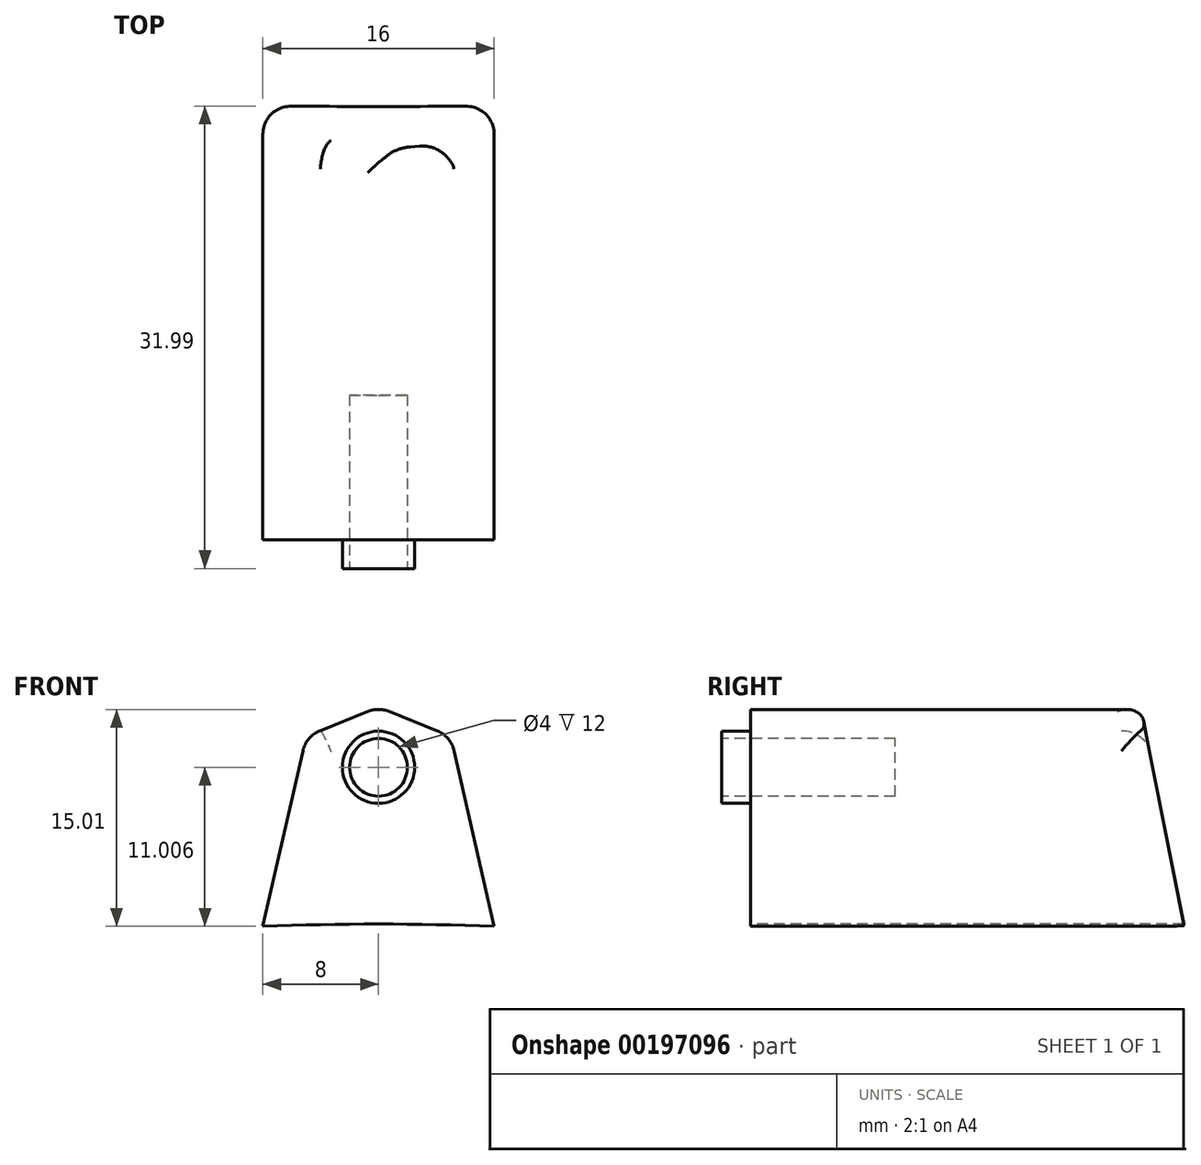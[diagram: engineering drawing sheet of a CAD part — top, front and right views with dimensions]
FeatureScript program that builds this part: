
annotation { "Feature Type Name" : "Feature", "Feature Type Description" : "" }
export const myFeature = defineFeature(function(context is Context, id is Id, definition is map)
    precondition{}
    {
        {
            var Q0;
            Q0=qCreatedBy(makeId("Front.planeOp"),FACE);
            var sketch = newSketch(context, id + "F0", { "sketchPlane" : qUnion([Q0])});
            skArc(sketch, "E0", {"start": v(8, 203.04) * mm, "mid": v(0, 203.2) * mm, "end": v(-8, 203.04) * mm});
            skLineSegment(sketch, "E1", {"start": v(0, 218.2) * mm, "end": v(5, 216.2) * mm});
            skLineSegment(sketch, "E2", {"start": v(5, 216.2) * mm, "end": v(8, 203.04) * mm});
            skLineSegment(sketch, "E3", {"start": v(0, 0) * mm, "end": v(0, 156.59) * mm, "construction": true});
            skLineSegment(sketch, "E4.MirrorCS", {"start": v(-5, 216.2) * mm, "end": v(-8, 203.04) * mm});
            skLineSegment(sketch, "E5.MirrorCS", {"start": v(0, 218.2) * mm, "end": v(-5, 216.2) * mm});
            skSolve(sketch);
        }
        {
            var Q0;
            Q0=makeQuery(id+"F0.imprint","IMPRINT",FACE,{"disambiguationData":[TD([[makeQuery(id+"F0.imprint","IMPRINT",EDGE,{"derivedFrom":sQuery(id+"F0.wireOp",EDGE,"E0")}),-1.0]])]});
            extrude(context, id + "F1", {"entities" : qUnion([Q0]), "oppositeDirection" : true, "depth" : 30 * mm});
        }
        {
            var Q0;
            Q0=qCreatedBy(makeId("Right.planeOp"),FACE);
            var sketch = newSketch(context, id + "F2", { "sketchPlane" : qUnion([Q0])});
            skLineSegment(sketch, "E6.0", {"start": v(30, 203.04) * mm, "end": v(0, 203.04) * mm});
            skLineSegment(sketch, "E7.0", {"start": v(30, 218.2) * mm, "end": v(0, 218.2) * mm});
            skLineSegment(sketch, "E8", {"start": v(30, 203.04) * mm, "end": v(27, 218.2) * mm});
            skLineSegment(sketch, "E9", {"start": v(30, 203.04) * mm, "end": v(30, 218.2) * mm});
            skSolve(sketch);
        }
        {
            var Q0;
            Q0 = qSketchRegion(id + "F2", true);
            extrude(context, id + "F3", {"entities" : qUnion([Q0]), "operationType" : NewBodyOperationType.REMOVE, "endBound" : BoundingType.SYMMETRIC, "depth" : 25 * mm});
        }
        {
            var Q0;
            Q0=makeQuery(id+"F1.opExtrude","SWEPT_EDGE",EDGE,{"disambiguationData":[OSD([sQuery(id+"F0.wireOp",EDGE,"E1"),sQuery(id+"F0.wireOp",EDGE,"E2")])]});
            var Q1;
            Q1=makeQuery(id+"F1.opExtrude","SWEPT_EDGE",EDGE,{"disambiguationData":[OSD([sQuery(id+"F0.wireOp",EDGE,"E1"),sQuery(id+"F0.wireOp",EDGE,"E5.MirrorCS")])]});
            var Q2;
            Q2=makeQuery(id+"F1.opExtrude","SWEPT_EDGE",EDGE,{"disambiguationData":[OSD([sQuery(id+"F0.wireOp",EDGE,"E4.MirrorCS"),sQuery(id+"F0.wireOp",EDGE,"E5.MirrorCS")])]});
            var Q3;
            Q3=makeQuery(id+"F3.boolean.opBoolean","INTERSECT",EDGE,{"derivedFrom":[makeQuery(id+"F1.opExtrude","SWEPT_FACE",FACE,{"disambiguationData":[OSD([sQuery(id+"F0.wireOp",EDGE,"E4.MirrorCS")])]}),makeQuery(id+"F3.opExtrude","SWEPT_FACE",FACE,{"disambiguationData":[OSD([sQuery(id+"F2.wireOp",EDGE,"E8")])]})]});
            var Q4;
            Q4=makeQuery(id+"F3.boolean.opBoolean","INTERSECT",EDGE,{"derivedFrom":[makeQuery(id+"F1.opExtrude","SWEPT_FACE",FACE,{"disambiguationData":[OSD([sQuery(id+"F0.wireOp",EDGE,"E5.MirrorCS")])]}),makeQuery(id+"F3.opExtrude","SWEPT_FACE",FACE,{"disambiguationData":[OSD([sQuery(id+"F2.wireOp",EDGE,"E8")])]})]});
            var Q5;
            Q5=makeQuery(id+"F3.boolean.opBoolean","INTERSECT",EDGE,{"derivedFrom":[makeQuery(id+"F1.opExtrude","SWEPT_FACE",FACE,{"disambiguationData":[OSD([sQuery(id+"F0.wireOp",EDGE,"E2")])]}),makeQuery(id+"F3.opExtrude","SWEPT_FACE",FACE,{"disambiguationData":[OSD([sQuery(id+"F2.wireOp",EDGE,"E8")])]})]});
            fillet(context, id + "F4", {"entities" : qUnion([Q0, Q1, Q2, Q3, Q4, Q5]), "radius" : 2 * mm, "tangentPropagation" : true, "allowEdgeOverflow" : false});
        }
        {
            var Q0;
            Q0=makeQuery(id+"F1.opExtrude","CAP_FACE",FACE,{"disambiguationData":[OSD([sQuery(id+"F0.wireOp",EDGE,"E0"),sQuery(id+"F0.wireOp",EDGE,"E1"),sQuery(id+"F0.wireOp",EDGE,"E2"),sQuery(id+"F0.wireOp",EDGE,"E4.MirrorCS"),sQuery(id+"F0.wireOp",EDGE,"E5.MirrorCS")])],"isStart":true});
            var sketch = newSketch(context, id + "F5", { "sketchPlane" : qUnion([Q0])});
            skCircle(sketch, "E10", {"center": v(0, 214.05) * mm, "radius": 2 * mm});
            skSolve(sketch);
        }
        {
            var Q0;
            Q0=makeQuery(id+"F5.imprint","IMPRINT",FACE,{"disambiguationData":[TD([[makeQuery(id+"F5.imprint","IMPRINT",EDGE,{"derivedFrom":sQuery(id+"F5.wireOp",EDGE,"E10")}),1.0]])]});
            extrude(context, id + "F6", {"entities" : qUnion([Q0]), "operationType" : NewBodyOperationType.REMOVE, "oppositeDirection" : true, "depth" : 10 * mm});
        }
        {
            var Q0;
            Q0=makeQuery(id+"F1.opExtrude","CAP_FACE",FACE,{"disambiguationData":[OSD([sQuery(id+"F0.wireOp",EDGE,"E0"),sQuery(id+"F0.wireOp",EDGE,"E1"),sQuery(id+"F0.wireOp",EDGE,"E2"),sQuery(id+"F0.wireOp",EDGE,"E4.MirrorCS"),sQuery(id+"F0.wireOp",EDGE,"E5.MirrorCS")])],"isStart":true});
            var sketch = newSketch(context, id + "F7", { "sketchPlane" : qUnion([Q0])});
            skCircle(sketch, "E11.0", {"center": v(0, 214.05) * mm, "radius": 2.5 * mm});
            skSolve(sketch);
        }
        {
            var Q0;
            Q0=makeQuery(id+"F7.imprint","IMPRINT",FACE,{"disambiguationData":[TD([[makeQuery(id+"F7.imprint","IMPRINT",EDGE,{"derivedFrom":sQuery(id+"F7.wireOp",EDGE,"E11.0")}),1.0]])]});
            extrude(context, id + "F8", {"entities" : qUnion([Q0]), "operationType" : NewBodyOperationType.ADD, "depth" : 2 * mm});
        }
    });
